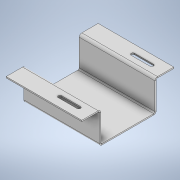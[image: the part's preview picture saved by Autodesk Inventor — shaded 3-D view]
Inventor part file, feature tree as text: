
AUTODESK INVENTOR PART (.ipt)
format: ipt  version: 2020 (Build 240168000, 168)  size: 192,000 bytes
history: native  units: mm
features: sheet_metal_op x13, sketch x7, other x7
ambient origin geometry x8: Origin, YZ Plane, XZ Plane, XY Plane, X Axis, Y Axis, Z Axis, Center Point
bodies: Solid1 (feature_tree)
feature tree (27):
  sheet_metal_op  "Face1"
  sheet_metal_op  "Flange5"
  sheet_metal_op  "Flange6"
  sheet_metal_op  "Flange7"
  sheet_metal_op  "Flange8"
  sketch  "Sketch1"  dims[d0=2.0mm]
  other  "Plate1"
  sketch  "Sketch6"  dims[d41=120.0mm]
  other  "Plate6"
  sheet_metal_op  "Bend5"
  sheet_metal_op  "Corner5"
  sketch  "Sketch7"  dims[d42=30.0mm]
  other  "Plate7"
  sheet_metal_op  "Bend6"
  sheet_metal_op  "Corner6"
  sketch  "Sketch8"  dims[d43=2.0mm]
  other  "Plate8"
  sheet_metal_op  "Bend7"
  sheet_metal_op  "Corner7"
  sketch  "Sketch9"  dims[d44=1.0mm]
  other  "Plate9"
  sheet_metal_op  "Bend8"
  sheet_metal_op  "Corner8"
  sketch  "Sketch15"  dims[d45=4.0mm]
  sketch  "Sketch16"  dims[d46=2.0mm d47=50.0mm d48=90.0deg d49=2.0mm d50=8.0mm d51=2.0mm d52=2.0mm d53=2.0mm d54=1.0mm d55=4.0mm d56=2.0mm d57=90.0mm d58=90.0deg d59=2.0mm d60=8.0mm d61=2.0mm d62=2.0mm d63=2.0mm d64=1.0mm d65=4.0mm d66=2.0mm d67=50.0mm d68=90.0deg d69=2.0mm d70=8.0mm d71=2.0mm d72=2.0mm d73=2.0mm d74=1.0mm d75=4.0mm d76=2.0mm d77=30.0mm d78=90.0deg d79=2.0mm d80=8.0mm d81=2.0mm d82=2.0mm d130=20.0mm d131=15.0mm d132=30.0mm d133=5.5mm d134=2.0mm d135=0.0mm d136=20.0mm d137=15.0mm d138=5.5mm d139=30.0mm d140=2.0mm d141=0.0mm]
  other  "Cut3"
  other  "Cut4"
